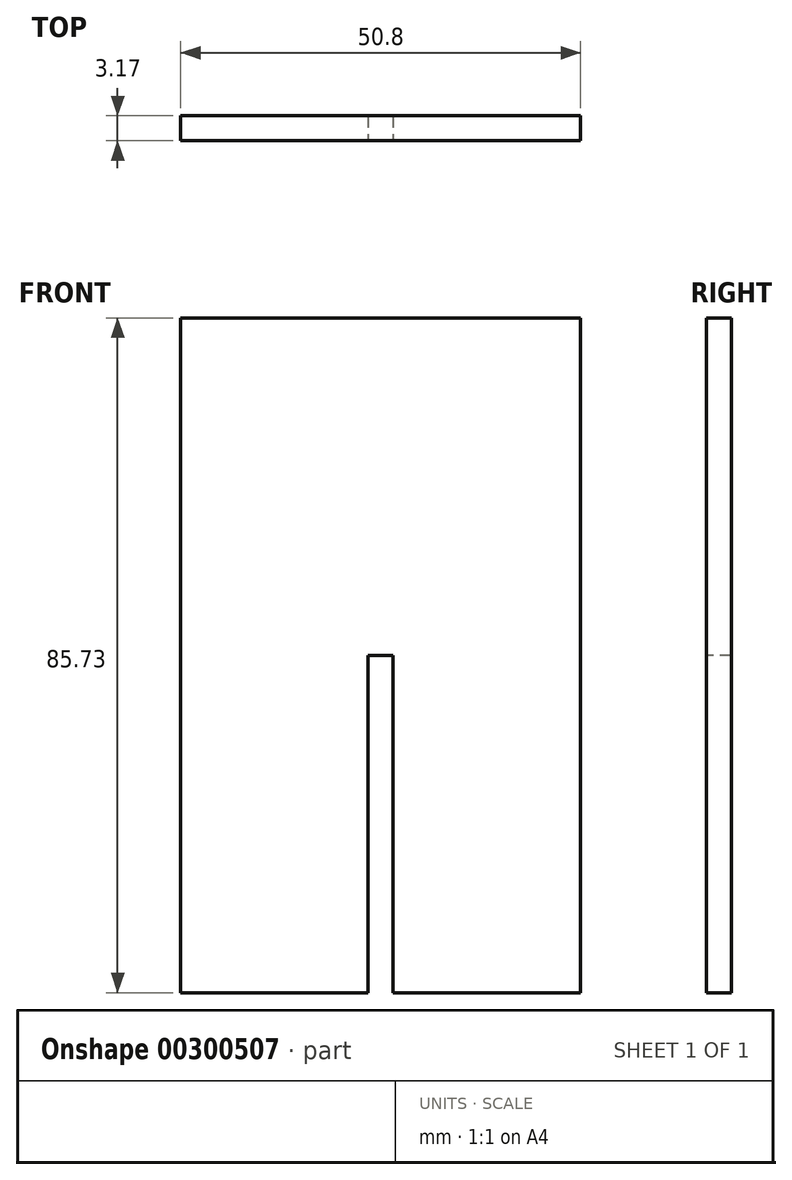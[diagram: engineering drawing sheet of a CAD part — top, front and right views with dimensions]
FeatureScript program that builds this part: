
annotation { "Feature Type Name" : "Feature", "Feature Type Description" : "" }
export const myFeature = defineFeature(function(context is Context, id is Id, definition is map)
    precondition{}
    {
        {
            var Q0;
            Q0=qCreatedBy(makeId("Front.planeOp"),FACE);
            var sketch = newSketch(context, id + "F0", { "sketchPlane" : qUnion([Q0])});
            skLineSegment(sketch, "E0.bottom", {"start": v(-28.6, 44.42) * mm, "end": v(22.2, 44.42) * mm});
            skLineSegment(sketch, "E0.top", {"start": v(-28.6, -41.3) * mm, "end": v(22.2, -41.3) * mm});
            skLineSegment(sketch, "E0.left", {"start": v(-28.6, 44.42) * mm, "end": v(-28.6, -41.3) * mm});
            skLineSegment(sketch, "E0.right", {"start": v(22.2, 44.42) * mm, "end": v(22.2, -41.3) * mm});
            skSolve(sketch);
        }
        {
            var Q0;
            Q0 = qSketchRegion(id + "F0", true);
            extrude(context, id + "F1", {"entities" : qUnion([Q0]), "depth" : 3.17 * mm});
        }
        {
            var Q0;
            Q0=makeQuery(id+"F1.opExtrude","CAP_FACE",FACE,{"disambiguationData":[OSD([sQuery(id+"F0.wireOp",EDGE,"E0.bottom"),sQuery(id+"F0.wireOp",EDGE,"E0.top"),sQuery(id+"F0.wireOp",EDGE,"E0.left"),sQuery(id+"F0.wireOp",EDGE,"E0.right")])],"isStart":false});
            var sketch = newSketch(context, id + "F2", { "sketchPlane" : qUnion([Q0])});
            skLineSegment(sketch, "E1", {"start": v(-3.2, 44.42) * mm, "end": v(-3.2, -41.3) * mm});
            skLineSegment(sketch, "E2.bottom", {"start": v(-3.2, -41.3) * mm, "end": v(-4.78, -41.3) * mm});
            skLineSegment(sketch, "E2.top", {"start": v(-3.2, 1.56) * mm, "end": v(-4.78, 1.56) * mm});
            skLineSegment(sketch, "E2.left", {"start": v(-3.2, -41.3) * mm, "end": v(-3.2, 1.56) * mm});
            skLineSegment(sketch, "E2.right", {"start": v(-4.78, -41.3) * mm, "end": v(-4.78, 1.56) * mm});
            skLineSegment(sketch, "E3.bottom", {"start": v(-3.2, -41.3) * mm, "end": v(-1.6, -41.3) * mm});
            skLineSegment(sketch, "E3.top", {"start": v(-3.2, 1.56) * mm, "end": v(-1.6, 1.56) * mm});
            skLineSegment(sketch, "E3.right", {"start": v(-1.6, -41.3) * mm, "end": v(-1.6, 1.56) * mm});
            skSolve(sketch);
        }
        {
            var Q0;
            Q0=makeQuery(id+"F2.imprint","IMPRINT",FACE,{"disambiguationData":[TD([[makeQuery(id+"F2.imprint","IMPRINT",EDGE,{"derivedFrom":sQuery(id+"F2.wireOp",EDGE,"E2.bottom")}),1.0]])]});
            var Q1;
            Q1=makeQuery(id+"F2.imprint","IMPRINT",FACE,{"disambiguationData":[TD([[makeQuery(id+"F2.imprint","IMPRINT",EDGE,{"derivedFrom":sQuery(id+"F2.wireOp",EDGE,"E3.bottom")}),1.0]])]});
            extrude(context, id + "F3", {"entities" : qUnion([Q0, Q1]), "operationType" : NewBodyOperationType.REMOVE, "endBound" : BoundingType.THROUGH_ALL, "oppositeDirection" : true, "depth" : 3.17 * mm});
        }
    });
